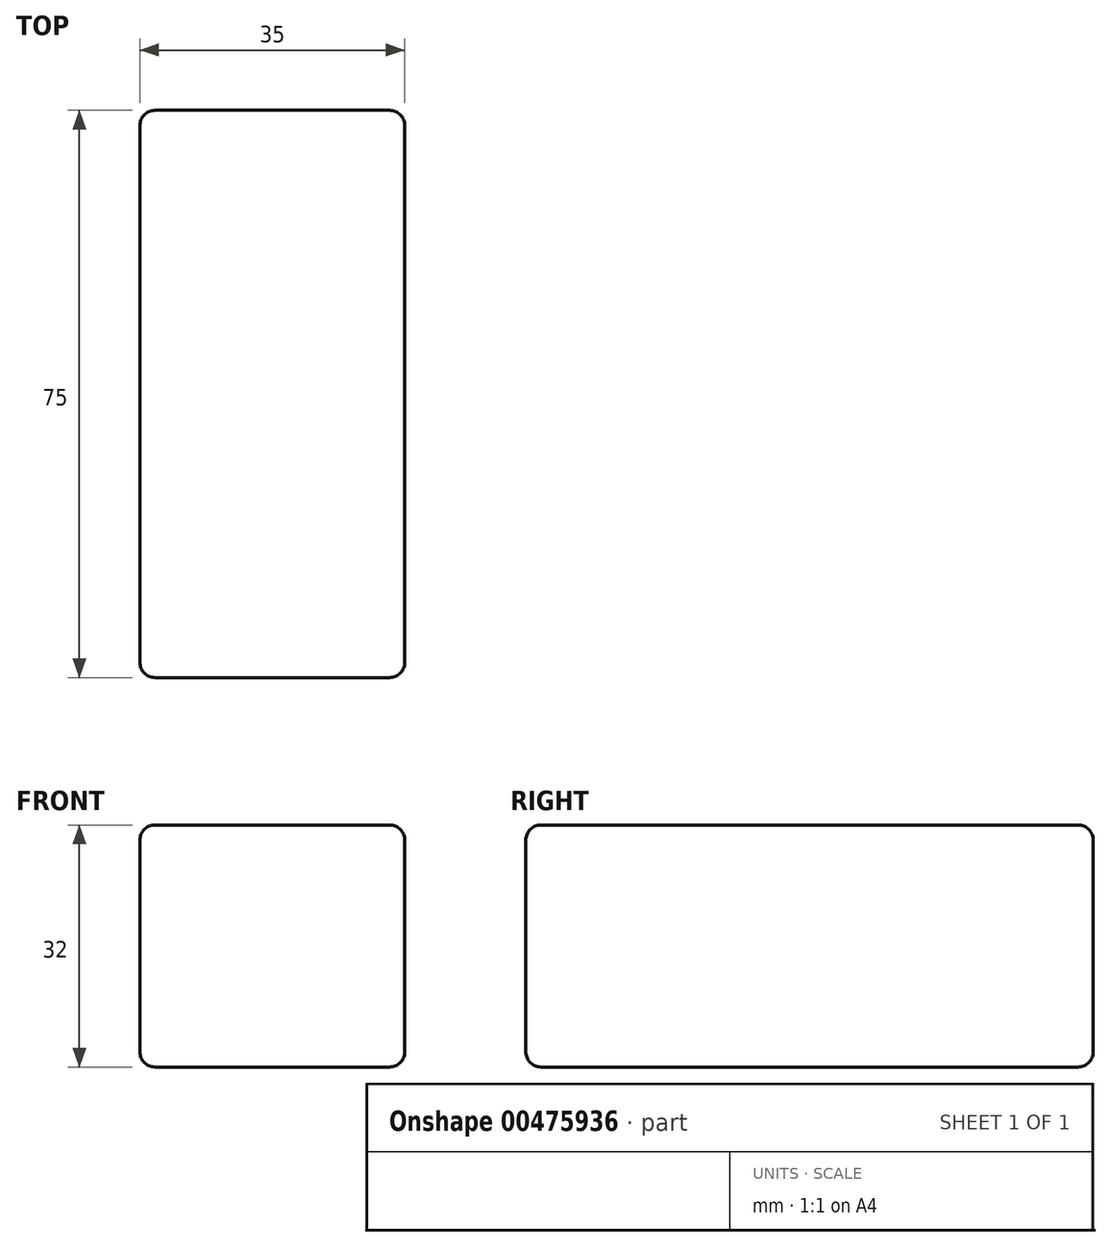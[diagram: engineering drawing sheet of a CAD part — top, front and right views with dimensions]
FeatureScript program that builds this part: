
annotation { "Feature Type Name" : "Feature", "Feature Type Description" : "" }
export const myFeature = defineFeature(function(context is Context, id is Id, definition is map)
    precondition{}
    {
        {
            var Q0;
            Q0=qCreatedBy(makeId("Top.planeOp"),FACE);
            var sketch = newSketch(context, id + "F0", { "sketchPlane" : qUnion([Q0])});
            skLineSegment(sketch, "E0.bottom", {"start": v(17.5, 37.5) * mm, "end": v(-17.5, 37.5) * mm});
            skLineSegment(sketch, "E0.top", {"start": v(17.5, -37.5) * mm, "end": v(-17.5, -37.5) * mm});
            skLineSegment(sketch, "E0.left", {"start": v(17.5, 37.5) * mm, "end": v(17.5, -37.5) * mm});
            skLineSegment(sketch, "E0.right", {"start": v(-17.5, 37.5) * mm, "end": v(-17.5, -37.5) * mm});
            skPoint(sketch, "E0.middle", {"position": v(0, 0) * mm});
            skSolve(sketch);
        }
        {
            var Q0;
            Q0 = qSketchRegion(id + "F0", true);
            extrude(context, id + "F1", {"entities" : qUnion([Q0]), "endBound" : BoundingType.SYMMETRIC, "depth" : 32 * mm});
        }
        {
            var Q0;
            Q0=makeQuery(id+"F1.opExtrude","SWEPT_FACE",FACE,{"disambiguationData":[OSD([sQuery(id+"F0.wireOp",EDGE,"E0.top")])]});
            var Q1;
            Q1=makeQuery(id+"F1.opExtrude","SWEPT_FACE",FACE,{"disambiguationData":[OSD([sQuery(id+"F0.wireOp",EDGE,"E0.left")])]});
            var Q2;
            Q2=makeQuery(id+"F1.opExtrude","SWEPT_FACE",FACE,{"disambiguationData":[OSD([sQuery(id+"F0.wireOp",EDGE,"E0.right")])]});
            var Q3;
            Q3=makeQuery(id+"F1.opExtrude","CAP_FACE",FACE,{"disambiguationData":[OSD([sQuery(id+"F0.wireOp",EDGE,"E0.bottom"),sQuery(id+"F0.wireOp",EDGE,"E0.top"),sQuery(id+"F0.wireOp",EDGE,"E0.left"),sQuery(id+"F0.wireOp",EDGE,"E0.right")])],"isStart":true});
            var Q4;
            Q4=makeQuery(id+"F1.opExtrude","CAP_FACE",FACE,{"disambiguationData":[OSD([sQuery(id+"F0.wireOp",EDGE,"E0.bottom"),sQuery(id+"F0.wireOp",EDGE,"E0.top"),sQuery(id+"F0.wireOp",EDGE,"E0.left"),sQuery(id+"F0.wireOp",EDGE,"E0.right")])],"isStart":false});
            fillet(context, id + "F2", {"entities" : qUnion([Q0, Q1, Q2, Q3, Q4]), "radius" : 2 * mm, "tangentPropagation" : true, "allowEdgeOverflow" : false});
        }
    });
